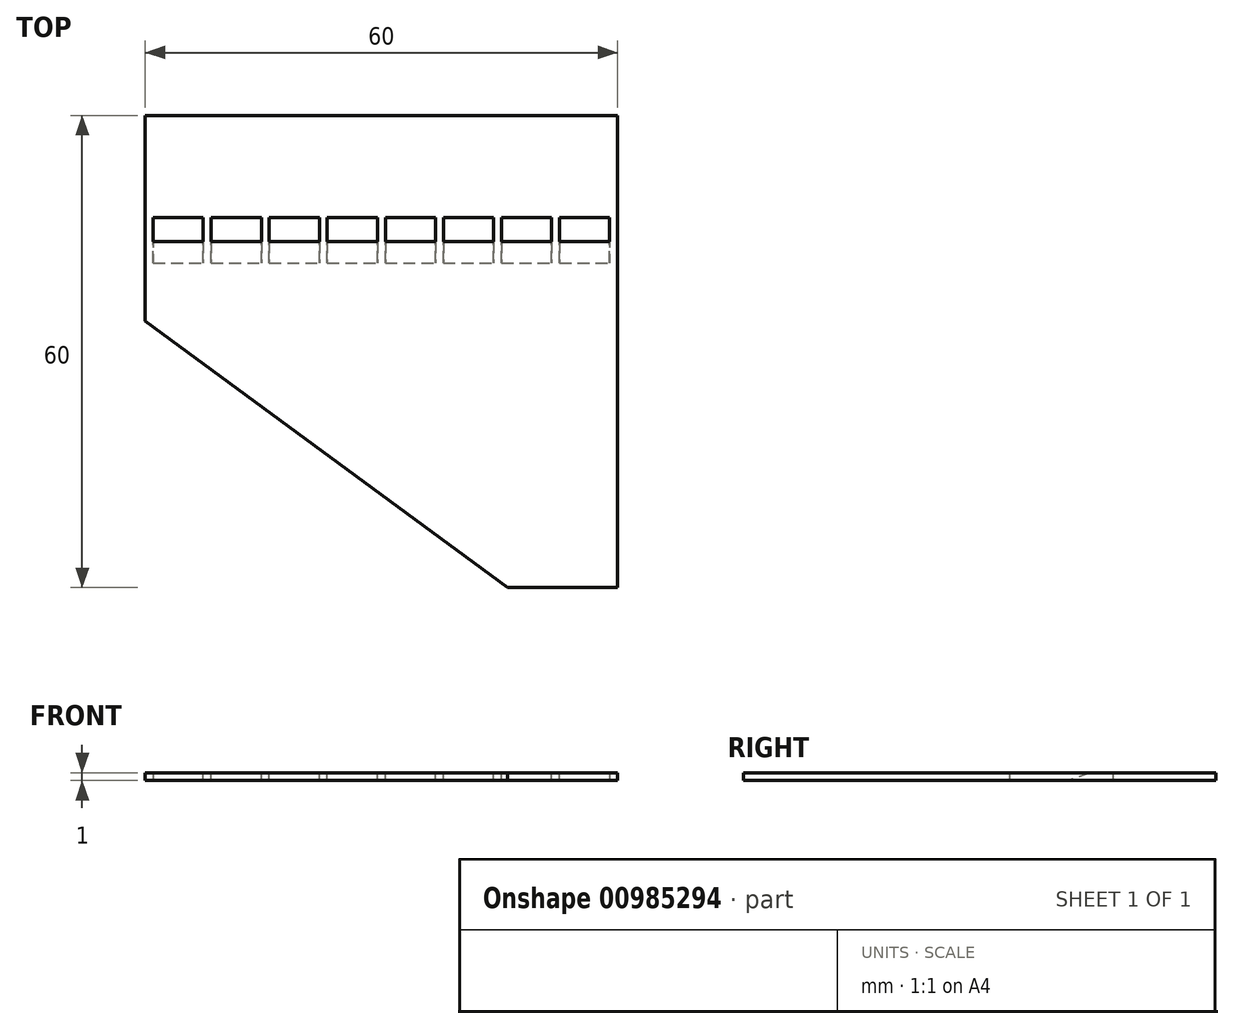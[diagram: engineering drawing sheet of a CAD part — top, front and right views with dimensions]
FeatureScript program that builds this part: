
annotation { "Feature Type Name" : "Feature", "Feature Type Description" : "" }
export const myFeature = defineFeature(function(context is Context, id is Id, definition is map)
    precondition{}
    {
        {
            var Q0;
            Q0=qCreatedBy(makeId("Top.planeOp"),FACE);
            var sketch = newSketch(context, id + "F0", { "sketchPlane" : qUnion([Q0])});
            skLineSegment(sketch, "E0.bottom", {"start": v(30, -30) * mm, "end": v(-30, -30) * mm});
            skLineSegment(sketch, "E0.top", {"start": v(30, 30) * mm, "end": v(-30, 30) * mm});
            skLineSegment(sketch, "E0.left", {"start": v(30, -30) * mm, "end": v(30, 30) * mm});
            skLineSegment(sketch, "E0.right", {"start": v(-30, -30) * mm, "end": v(-30, 30) * mm});
            skPoint(sketch, "E0.middle", {"position": v(0, 0) * mm});
            skSolve(sketch);
        }
        {
            var Q0;
            Q0=qSketchRegion(id+"F0",true);
            extrude(context, id + "F1", {"entities" : qUnion([Q0]), "depth" : 1 * mm, "offsetDistance" : 25 * mm});
        }
        {
            var Q0;
            Q0=qCreatedBy(makeId("Right.planeOp"),FACE);
            var sketch = newSketch(context, id + "F2", { "sketchPlane" : qUnion([Q0])});
            skLineSegment(sketch, "E1", {"start": v(0, 0.54) * mm, "end": v(25.35, 0.54) * mm, "construction": true});
            skLineSegment(sketch, "E2", {"start": v(0, 0) * mm, "end": v(0, 1) * mm, "construction": true});
            skLineSegment(sketch, "E3.MirrorCS", {"start": v(17, 0) * mm, "end": v(11.25, 0) * mm});
            skLineSegment(sketch, "E4.MirrorCS", {"start": v(14, 1) * mm, "end": v(17, 1) * mm});
            skLineSegment(sketch, "E5.MirrorCS", {"start": v(17, 1) * mm, "end": v(17, 0) * mm});
            skLineSegment(sketch, "E6.MirrorCS", {"start": v(11.25, 0) * mm, "end": v(14, 1) * mm});
            skSolve(sketch);
        }
        {
            var Q0;
            Q0=makeQuery(id+"F1.opExtrude","CAP_FACE",FACE,{"disambiguationData":[OSD([sQuery(id+"F0.wireOp",EDGE,"E0.bottom"),sQuery(id+"F0.wireOp",EDGE,"E0.top"),sQuery(id+"F0.wireOp",EDGE,"E0.left"),sQuery(id+"F0.wireOp",EDGE,"E0.right")])],"isStart":false});
            var sketch = newSketch(context, id + "F3", { "sketchPlane" : qUnion([Q0])});
            skLineSegment(sketch, "E7.MirrorCS", {"start": v(16, -30) * mm, "end": v(-30, 3.86) * mm});
            skSolve(sketch);
        }
        {
            var Q0;
            {var subQ0=sQuery(id+"F3.wireOp",EDGE,"E7.MirrorCS");Q0=makeQuery(id+"F3.imprint","IMPRINT",FACE,{"disambiguationData":[TD([[makeQuery(id+"F3.imprint","IMPRINT",EDGE,{"derivedFrom":subQ0}),1.0]])]});}
            var Q1;
            Q1=makeQuery(id+"F1.opExtrude","CAP_FACE",FACE,{"disambiguationData":[OSD([sQuery(id+"F0.wireOp",EDGE,"E0.bottom"),sQuery(id+"F0.wireOp",EDGE,"E0.top"),sQuery(id+"F0.wireOp",EDGE,"E0.left"),sQuery(id+"F0.wireOp",EDGE,"E0.right")])],"isStart":true});
            extrude(context, id + "F4", {"entities" : qUnion([Q0]), "operationType" : NewBodyOperationType.REMOVE, "endBound" : BoundingType.UP_TO_SURFACE, "oppositeDirection" : true, "depth" : 25 * mm, "endBoundEntityFace" : qUnion([Q1]), "offsetDistance" : 25 * mm});
        }
        {
            var Q0;
            Q0 = qSketchRegion(id + "F2", true);
            extrude(context, id + "F5", {"entities" : qUnion([Q0]), "operationType" : NewBodyOperationType.REMOVE, "endBound" : BoundingType.SYMMETRIC, "oppositeDirection" : true, "depth" : 58 * mm, "offsetDistance" : 25 * mm});
        }
        {
            var Q0;
            Q0=makeQuery(id+"F5.boolean.opBoolean","COPY",FACE,{"derivedFrom":makeQuery(id+"F5.opExtrude","SWEPT_FACE",FACE,{"disambiguationData":[OSD([sQuery(id+"F2.wireOp",EDGE,"E5.MirrorCS")])]})});
            var sketch = newSketch(context, id + "F6", { "sketchPlane" : qUnion([Q0])});
            skLineSegment(sketch, "E8", {"start": v(0, 0) * mm, "end": v(0, 6.07) * mm, "construction": true});
            skLineSegment(sketch, "E9", {"start": v(-0.5, 0) * mm, "end": v(-0.5, 1) * mm});
            skLineSegment(sketch, "E10", {"start": v(-14.25, 0) * mm, "end": v(-14.25, 1) * mm});
            skLineSegment(sketch, "E11", {"start": v(-15.25, 0) * mm, "end": v(-15.25, 1) * mm});
            skLineSegment(sketch, "E12", {"start": v(-22.62, 0) * mm, "end": v(-22.62, 1) * mm});
            skLineSegment(sketch, "E13", {"start": v(-6.88, 0) * mm, "end": v(-6.88, 1) * mm});
            skLineSegment(sketch, "E14", {"start": v(-7.88, 0) * mm, "end": v(-7.88, 1) * mm});
            skLineSegment(sketch, "E15", {"start": v(-21.62, 0) * mm, "end": v(-21.62, 1) * mm});
            skLineSegment(sketch, "E16", {"start": v(0.5, 0) * mm, "end": v(-0.5, 0) * mm, "construction": true});
            skLineSegment(sketch, "E17", {"start": v(-29, 0) * mm, "end": v(-22.62, 0) * mm});
            skLineSegment(sketch, "E18", {"start": v(-22.62, 0) * mm, "end": v(-21.62, 0) * mm});
            skLineSegment(sketch, "E19", {"start": v(-21.62, 0) * mm, "end": v(-15.25, 0) * mm});
            skLineSegment(sketch, "E20", {"start": v(-15.25, 0) * mm, "end": v(-14.25, 0) * mm});
            skLineSegment(sketch, "E21", {"start": v(-14.25, 0) * mm, "end": v(-7.88, 0) * mm});
            skLineSegment(sketch, "E22", {"start": v(-7.88, 0) * mm, "end": v(-6.88, 0) * mm});
            skLineSegment(sketch, "E23", {"start": v(-6.88, 0) * mm, "end": v(-0.5, 0) * mm});
            skLineSegment(sketch, "E24.MirrorCS", {"start": v(7.88, 0) * mm, "end": v(6.88, 0) * mm});
            skLineSegment(sketch, "E25.MirrorCS", {"start": v(15.25, 0) * mm, "end": v(14.25, 0) * mm});
            skLineSegment(sketch, "E26.MirrorCS", {"start": v(22.62, 0) * mm, "end": v(21.62, 0) * mm});
            skLineSegment(sketch, "E27.MirrorCS", {"start": v(21.62, 0) * mm, "end": v(21.62, 1) * mm});
            skLineSegment(sketch, "E28.MirrorCS", {"start": v(0.5, 0) * mm, "end": v(0.5, 1) * mm});
            skLineSegment(sketch, "E29.MirrorCS", {"start": v(14.25, 0) * mm, "end": v(14.25, 1) * mm});
            skLineSegment(sketch, "E30.MirrorCS", {"start": v(6.88, 0) * mm, "end": v(6.88, 1) * mm});
            skLineSegment(sketch, "E31.MirrorCS", {"start": v(22.62, 0) * mm, "end": v(22.62, 1) * mm});
            skLineSegment(sketch, "E32.MirrorCS", {"start": v(7.88, 0) * mm, "end": v(7.88, 1) * mm});
            skLineSegment(sketch, "E33.MirrorCS", {"start": v(15.25, 0) * mm, "end": v(15.25, 1) * mm});
            skLineSegment(sketch, "E34.MirrorCS", {"start": v(6.88, 0) * mm, "end": v(0.5, 0) * mm});
            skLineSegment(sketch, "E35.MirrorCS", {"start": v(29, 0) * mm, "end": v(22.62, 0) * mm});
            skLineSegment(sketch, "E36.MirrorCS", {"start": v(21.62, 0) * mm, "end": v(15.25, 0) * mm});
            skLineSegment(sketch, "E37.MirrorCS", {"start": v(14.25, 0) * mm, "end": v(7.88, 0) * mm});
            skSolve(sketch);
        }
        {
            var Q0;
            {var subQ0=sQuery(id+"F6.wireOp",EDGE,"E12");Q0=makeQuery(id+"F6.imprint","IMPRINT",FACE,{"disambiguationData":[TD([[makeQuery(id+"F6.imprint","IMPRINT",EDGE,{"derivedFrom":subQ0}),-1.0]])]});}
            var Q1;
            {var subQ0=sQuery(id+"F6.wireOp",EDGE,"E10");Q1=makeQuery(id+"F6.imprint","IMPRINT",FACE,{"disambiguationData":[TD([[makeQuery(id+"F6.imprint","IMPRINT",EDGE,{"derivedFrom":subQ0}),1.0]])]});}
            var Q2;
            {var subQ0=sQuery(id+"F6.wireOp",EDGE,"E13");Q2=makeQuery(id+"F6.imprint","IMPRINT",FACE,{"disambiguationData":[TD([[makeQuery(id+"F6.imprint","IMPRINT",EDGE,{"derivedFrom":subQ0}),1.0]])]});}
            var Q3;
            {var subQ0=sQuery(id+"F6.wireOp",EDGE,"E9");Q3=makeQuery(id+"F6.imprint","IMPRINT",FACE,{"disambiguationData":[TD([[makeQuery(id+"F6.imprint","IMPRINT",EDGE,{"derivedFrom":subQ0}),-1.0]])]});}
            var Q4;
            Q4=makeQuery(id+"F6.imprint","IMPRINT",FACE,{"disambiguationData":[TD([[makeQuery(id+"F6.imprint","IMPRINT",EDGE,{"derivedFrom":sQuery(id+"F6.wireOp",EDGE,"E24.MirrorCS")}),1.0]])]});
            var Q5;
            Q5=makeQuery(id+"F6.imprint","IMPRINT",FACE,{"disambiguationData":[TD([[makeQuery(id+"F6.imprint","IMPRINT",EDGE,{"derivedFrom":sQuery(id+"F6.wireOp",EDGE,"E25.MirrorCS")}),1.0]])]});
            var Q6;
            Q6=makeQuery(id+"F6.imprint","IMPRINT",FACE,{"disambiguationData":[TD([[makeQuery(id+"F6.imprint","IMPRINT",EDGE,{"derivedFrom":sQuery(id+"F6.wireOp",EDGE,"E26.MirrorCS")}),1.0]])]});
            extrude(context, id + "F7", {"entities" : qUnion([Q0, Q1, Q2, Q3, Q4, Q5, Q6]), "operationType" : NewBodyOperationType.ADD, "endBound" : BoundingType.UP_TO_NEXT, "depth" : 25 * mm, "offsetDistance" : 25 * mm});
        }
    });
